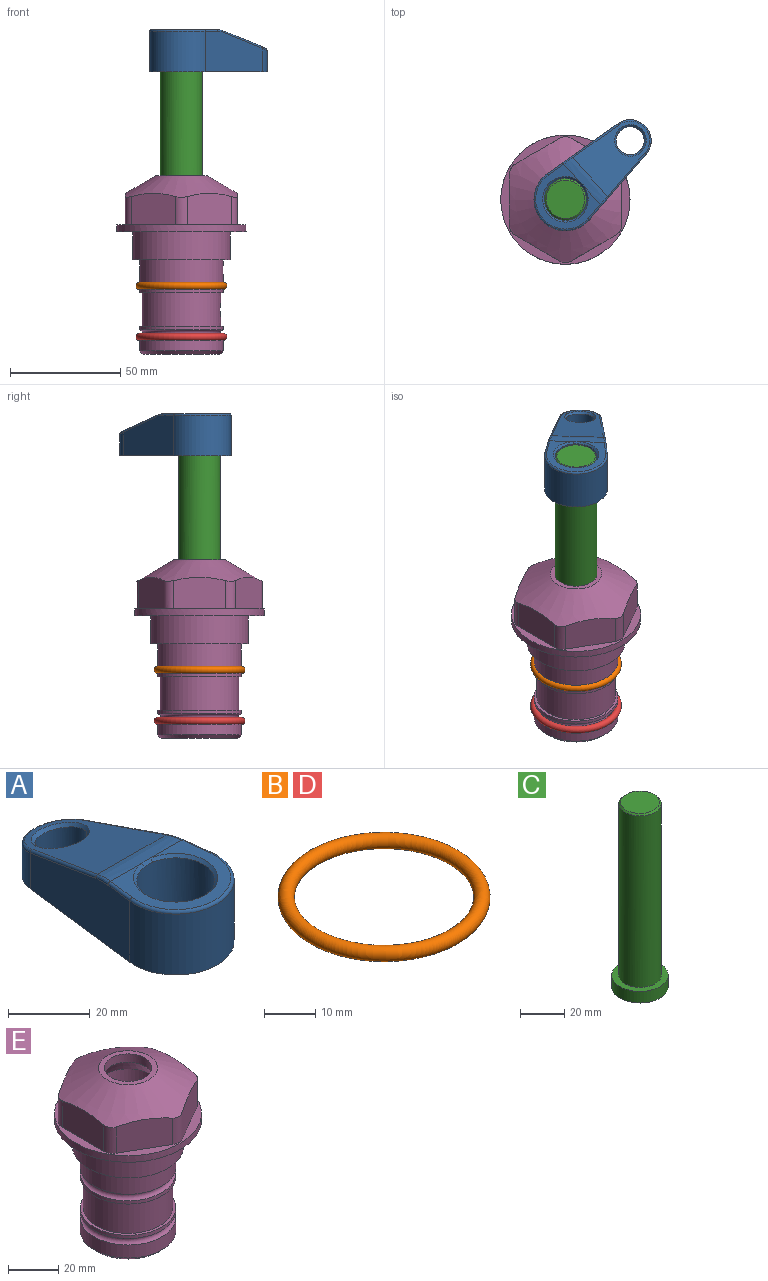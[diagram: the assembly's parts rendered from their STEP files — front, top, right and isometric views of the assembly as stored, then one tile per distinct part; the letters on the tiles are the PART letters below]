
ASSEMBLY  parts=5 mates=4
PART A: 31 faces, bbox 31.7x65.5x19.8 mm
  f0: plane 39.12x18.26mm, normal (0.99,0.12,0), area 612.2mm2, adj f1,f4,f7,f11,f13,f15
  f1: cylinder r=9.53mm len=18.91mm, axis (0,0,-1), area 296.1mm2, adj f0,f2,f7,f17
  f2: plane 39.12x18.26mm, normal (-0.99,0.12,0), area 612.2mm2, adj f1,f4,f7,f12,f14,f16
  f3: cylinder r=6.35mm len=12.7mm, axis (0,0,-1), area 362.4mm2, adj f7,f18
  f4: cylinder r=14.29mm len=28.58mm, axis (0,0,-1), area 882.2mm2, adj f0,f2,f7,f10
  f5: cylinder r=9.53mm len=19.05mm, axis (0,0,-1), area 1092.6mm2, adj f7,f19,f20
  f6: plane 26.99x23.69mm, normal (0,0,1), area 216.2mm2, adj f9,f10,f11,f12,f19
  f7: plane 63.5x28.58mm, normal (0,0,-1), area 661.8mm2, adj f0,f1,f2,f3,f4,f5,f22,f23
  f8: plane 33.52x23.6mm, normal (0,0.26,0.97), area 486mm2, adj f9,f15,f16,f17,f18
  f9: cylinder r=19.05mm len=24.72mm, axis (1,0,0), area 120.4mm2, adj f6,f8,f13,f14,f20
  f10: torus R=13.49mm, axis (0,0,1), area 59mm2, adj f4,f6,f11,f12
  f11: cylinder r=0.79mm len=8.67mm, axis (0.12,-0.99,0), area 10.8mm2, adj f0,f6,f10,f13
  f12: cylinder r=0.79mm len=8.67mm, axis (0.12,0.99,0), area 10.8mm2, adj f2,f6,f10,f14
  f13: bspline ~4.95x1.42mm, area 6.1mm2, adj f0,f9,f11,f15
  f14: bspline ~4.95x1.42mm, area 6.1mm2, adj f2,f9,f12,f16
  f15: cylinder r=0.79mm len=25.95mm, axis (0.12,-0.96,0.26), area 32.9mm2, adj f0,f8,f13,f17
  f16: cylinder r=0.79mm len=25.95mm, axis (0.12,0.96,-0.26), area 32.9mm2, adj f2,f8,f14,f17
  f17: bspline ~18.91x8.38mm, area 30mm2, adj f1,f8,f15,f16
  f18: bspline ~14.29x14.29mm, area 48.3mm2, adj f3,f8
  f19: cone r=9.53mm half-angle=45deg, axis (0,0,1), area 66.5mm2, adj f5,f6,f20
  f20: bspline ~3.22x0.96mm, area 3.5mm2, adj f5,f9,f19
  f21: plane 2.75x2.72mm, normal (0,0,-1), area 2.9mm2, adj f23,f25,f28
  f22: plane 23.05x15.88mm, normal (-0.99,-0.12,0), area 323.6mm2, adj f7,f25,f26,f27,f28,f29
  f23: plane 23.05x15.88mm, normal (0.99,-0.12,0), area 323.6mm2, adj f7,f21,f25,f27,f28,f30
  f24: cylinder r=9.53mm len=10.69mm, axis (0,0,-1), area 114.7mm2, adj f7,f27,f29,f30
  f25: cylinder r=12.7mm len=20.59mm, axis (0,0,-1), area 381.1mm2, adj f7,f21,f22,f23,f26,f28
  f26: plane 2.75x2.72mm, normal (0,0,-1), area 2.9mm2, adj f22,f25,f28
  f27: plane 19.72x18.37mm, normal (0,-0.26,-0.97), area 291.8mm2, adj f22,f23,f24,f28,f29,f30
  f28: cylinder r=15.88mm len=19.92mm, axis (1,0,0), area 54.8mm2, adj f21,f22,f23,f25,f26,f27
  f29: cylinder r=1.59mm len=11mm, axis (0,0,-1), area 34.7mm2, adj f7,f22,f24,f27
  f30: cylinder r=1.59mm len=11mm, axis (0,0,-1), area 34.7mm2, adj f7,f23,f24,f27
PART B: 1 faces, bbox 44.7x44.7x3.2 mm
  f0: torus R=19.05mm, axis (0,0,1), area 1193.9mm2
PART C: 6 faces, bbox 25.4x25.4x101.6 mm
  f0: plane 17.46x17.46mm, normal (0,0,1), area 239.5mm2, adj f5
  f1: plane 25.4x25.4mm, normal (0,0,-1), area 506.7mm2, adj f2
  f2: cylinder r=12.7mm len=25.4mm, axis (0,0,1), area 506.7mm2, adj f1,f3
  f3: plane 25.4x25.4mm, normal (0,0,1), area 221.7mm2, adj f2,f4
  f4: cylinder r=9.53mm len=94.46mm, axis (0,0,1), area 5653mm2, adj f3,f5
  f5: cone r=8.73mm half-angle=45deg, axis (0,0,-1), area 64.4mm2, adj f0,f4
PART D: same geometry as B
PART E: 36 faces, bbox 58.7x58.7x81 mm
  f0: cylinder r=17.78mm len=35.56mm, axis (0,0,1), area 1670.8mm2, adj f23,f24,f31
  f1: cylinder r=19.05mm len=38.1mm, axis (0,0,1), area 1191.9mm2, adj f26,f27,f30
  f2: plane 58.66x58.66mm, normal (0,0,-1), area 1150.6mm2, adj f3,f28
  f3: cylinder r=29.33mm len=58.66mm, axis (0,0,-1), area 585.1mm2, adj f2,f4
  f4: plane 58.66x58.66mm, normal (0,0,1), area 475.9mm2, adj f3,f5,f6,f7,f8,f9,f10,f11
  f5: plane 20.32x14.34mm, normal (-0.5,0.87,0), area 324.4mm2, adj f4,f15,f16,f17
  f6: plane 20.32x14.34mm, normal (0.5,0.87,0), area 324.4mm2, adj f4,f14,f15,f17
  f7: plane 23.48x14.34mm, normal (1,0,0), area 324.4mm2, adj f4,f13,f14,f17
  f8: plane 20.32x14.34mm, normal (0.5,-0.87,0), area 324.4mm2, adj f4,f12,f13,f17
  f9: plane 20.32x14.34mm, normal (-0.5,-0.87,0), area 324.4mm2, adj f4,f11,f12,f17
  f10: plane 23.48x14.34mm, normal (-1,0,0), area 324.4mm2, adj f4,f11,f16,f17
  f11: cylinder r=5.08mm len=12.85mm, axis (0,0,-1), area 67.2mm2, adj f4,f9,f10,f17
  f12: cylinder r=5.08mm len=12.85mm, axis (0,0,-1), area 67.2mm2, adj f4,f8,f9,f17
  f13: cylinder r=5.08mm len=12.85mm, axis (0,0,-1), area 67.2mm2, adj f4,f7,f8,f17
  f14: cylinder r=5.08mm len=12.85mm, axis (0,0,-1), area 67.2mm2, adj f4,f6,f7,f17
  f15: cylinder r=5.08mm len=12.85mm, axis (0,0,-1), area 67.2mm2, adj f4,f5,f6,f17
  f16: cylinder r=5.08mm len=12.85mm, axis (0,0,-1), area 67.2mm2, adj f4,f5,f10,f17
  f17: cone r=11.73mm half-angle=60deg, axis (0,0,-1), area 2071.8mm2, adj f5,f6,f7,f8,f9,f10,f11,f12
  f18: plane 23.46x23.46mm, normal (0,0,1), area 147.4mm2, adj f17,f35
  f19: plane 34.93x34.93mm, normal (0,0,-1), area 958mm2, adj f29
  f20: cylinder r=19.05mm len=38.1mm, axis (0,0,1), area 760.1mm2, adj f21,f29
  f21: torus R=19.05mm, axis (0,0,1), area 565.3mm2, adj f20,f22
  f22: cylinder r=19.05mm len=38.1mm, axis (0,0,1), area 190mm2, adj f21,f23
  f23: plane 38.1x38.1mm, normal (0,0,1), area 146.9mm2, adj f0,f22
  f24: plane 38.1x38.1mm, normal (0,0,-1), area 146.9mm2, adj f0,f25
  f25: cylinder r=19.05mm len=38.1mm, axis (0,0,1), area 190mm2, adj f24,f26
  f26: torus R=19.05mm, axis (0,0,1), area 565.3mm2, adj f1,f25
  f27: plane 44.45x44.45mm, normal (0,0,-1), area 411.7mm2, adj f1,f28
  f28: cylinder r=22.23mm len=44.45mm, axis (0,0,1), area 1773.5mm2, adj f2,f27
  f29: cone r=19.05mm half-angle=45deg, axis (0,0,1), area 257.5mm2, adj f19,f20
  f30: cylinder r=3.17mm len=6.75mm, axis (-1,0,0), area 128mm2, adj f1,f33
  f31: cylinder r=3.17mm len=6.35mm, axis (-1,0,0), area 102.5mm2, adj f0,f33
  f32: plane 25.4x25.4mm, normal (0,0,1), area 506.7mm2, adj f33
  f33: cylinder r=12.7mm len=66.42mm, axis (0,0,-1), area 5236.2mm2, adj f30,f31,f32,f34
  f34: cone r=9.53mm half-angle=30deg, axis (0,0,-1), area 443.4mm2, adj f33,f35
  f35: cylinder r=9.53mm len=19.05mm, axis (0,0,-1), area 240.9mm2, adj f18,f34
PLACE A rot(axis=(0,0,-1),47.8deg) t=(0,0,28.35)mm
PLACE B at identity
PLACE C rot(axis=(0,0,-1),47.8deg) t=(0,0,27.55)mm
PLACE D t=(0,0,-23.18)mm
PLACE E at identity fixed
MATE cylindrical C.f2 <-> E.f0  axis (0,0,-1) through (0,0,-10.55)mm
MATE fastened A.f4 <-> C.f2  axis (0,0,1) through (0,0,91.05)mm
MATE fastened B.f0 <-> E.f0  axis (0,0,1) through (0,0,-24.51)mm
MATE fastened D.f0 <-> E.f0  axis (0,0,1) through (0,0,-47.69)mm
